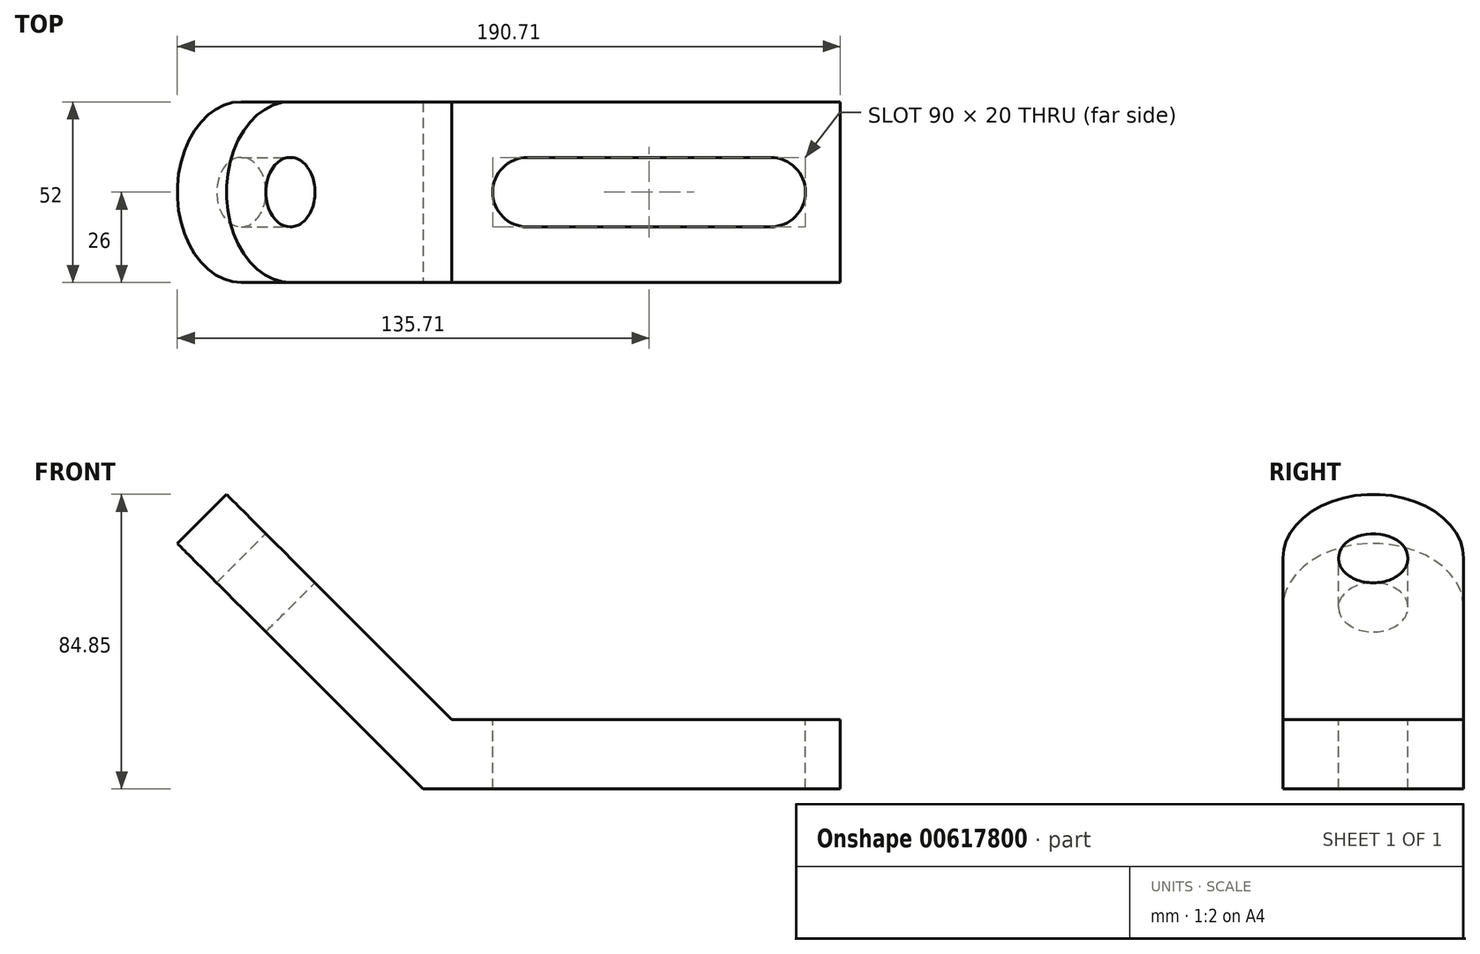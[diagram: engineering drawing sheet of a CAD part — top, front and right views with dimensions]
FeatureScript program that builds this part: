
annotation { "Feature Type Name" : "Feature", "Feature Type Description" : "" }
export const myFeature = defineFeature(function(context is Context, id is Id, definition is map)
    precondition{}
    {
        {
            var Q0;
            Q0=qCreatedBy(makeId("Top.planeOp"),FACE);
            var sketch = newSketch(context, id + "F0", { "sketchPlane" : qUnion([Q0])});
            skLineSegment(sketch, "E0.bottom", {"start": v(60, 26) * mm, "end": v(-60, 26) * mm});
            skLineSegment(sketch, "E0.top", {"start": v(60, -26) * mm, "end": v(-60, -26) * mm});
            skLineSegment(sketch, "E0.left", {"start": v(60, 26) * mm, "end": v(60, -26) * mm});
            skLineSegment(sketch, "E0.right", {"start": v(-60, 26) * mm, "end": v(-60, -26) * mm});
            skPoint(sketch, "E0.middle", {"position": v(0, 0) * mm});
            skSolve(sketch);
        }
        {
            var Q0;
            Q0=makeQuery(id+"F0.imprint","IMPRINT",FACE,{"disambiguationData":[TD([[makeQuery(id+"F0.imprint","IMPRINT",EDGE,{"derivedFrom":sQuery(id+"F0.wireOp",EDGE,"E0.bottom")}),1.0]])]});
            var sketch = newSketch(context, id + "F1", { "sketchPlane" : qUnion([Q0])});
            skLineSegment(sketch, "E1.bottom", {"start": v(-60, 26) * mm, "end": v(-134, 26) * mm});
            skLineSegment(sketch, "E1.top", {"start": v(-60, -26) * mm, "end": v(-134, -26) * mm});
            skLineSegment(sketch, "E1.left", {"start": v(-60, 26) * mm, "end": v(-60, -26) * mm});
            skLineSegment(sketch, "E1.right", {"start": v(-134, 26) * mm, "end": v(-134, -26) * mm});
            skArc(sketch, "E2", {"start": v(-134, 26) * mm, "mid": v(-160, 0) * mm, "end": v(-134, -26) * mm});
            skSolve(sketch);
        }
        {
            var Q0;
            Q0=makeQuery(id+"F1.imprint","IMPRINT",FACE,{"disambiguationData":[TD([[makeQuery(id+"F1.imprint","IMPRINT",EDGE,{"derivedFrom":sQuery(id+"F1.wireOp",EDGE,"E1.bottom")}),1.0]])]});
            var Q1;
            Q1=makeQuery(id+"F1.imprint","IMPRINT",FACE,{"disambiguationData":[TD([[makeQuery(id+"F1.imprint","IMPRINT",EDGE,{"derivedFrom":sQuery(id+"F1.wireOp",EDGE,"E1.right")}),-1.0]])]});
            extrude(context, id + "F2", {"entities" : qUnion([Q0, Q1]), "depth" : 20 * mm, "offsetDistance" : 25 * mm});
        }
        {
            var Q0;
            Q0=makeQuery(id+"F2.opExtrude","SWEPT_BODY",BODY,{"disambiguationData":[OSD([sQuery(id+"F1.wireOp",EDGE,"E1.bottom"),sQuery(id+"F1.wireOp",EDGE,"E1.top"),sQuery(id+"F1.wireOp",EDGE,"E1.left"),sQuery(id+"F1.wireOp",EDGE,"E1.right")])]});
            var Q1;
            Q1=sQuery(id+"F0.wireOp",EDGE,"E0.right");
            transform(context, id + "F3", {"entities" : qUnion([Q0]), "transformType" : TransformType.ROTATION, "transformAxis" : qUnion([Q1]), "angle" : 45 * degree, "oppositeDirection" : true, "makeCopy" : false});
        }
        {
            var Q0;
            Q0=makeQuery(id+"F0.imprint","IMPRINT",FACE,{"disambiguationData":[TD([[makeQuery(id+"F0.imprint","IMPRINT",EDGE,{"derivedFrom":sQuery(id+"F0.wireOp",EDGE,"E0.bottom")}),1.0]])]});
            extrude(context, id + "F4", {"entities" : qUnion([Q0]), "operationType" : NewBodyOperationType.ADD, "depth" : 20 * mm, "offsetDistance" : 25 * mm});
        }
        {
            var Q0;
            Q0=makeQuery(id+"F4.opExtrude","CAP_FACE",FACE,{"disambiguationData":[OSD([sQuery(id+"F0.wireOp",EDGE,"E0.bottom"),sQuery(id+"F0.wireOp",EDGE,"E0.top"),sQuery(id+"F0.wireOp",EDGE,"E0.left"),sQuery(id+"F0.wireOp",EDGE,"E0.right")])],"isStart":false});
            var sketch = newSketch(context, id + "F5", { "sketchPlane" : qUnion([Q0])});
            skLineSegment(sketch, "E3.bottom", {"start": v(-30, 10) * mm, "end": v(40, 10) * mm});
            skLineSegment(sketch, "E3.top", {"start": v(-30, -10) * mm, "end": v(40, -10) * mm});
            skLineSegment(sketch, "E3.left", {"start": v(-30, 10) * mm, "end": v(-30, -10) * mm});
            skLineSegment(sketch, "E3.right", {"start": v(40, 10) * mm, "end": v(40, -10) * mm});
            skPoint(sketch, "E3.middle", {"position": v(5, 0) * mm});
            skArc(sketch, "E4", {"start": v(40, -10) * mm, "mid": v(50, 0) * mm, "end": v(40, 10) * mm});
            skArc(sketch, "E5", {"start": v(-30, 10) * mm, "mid": v(-40, 0) * mm, "end": v(-30, -10) * mm});
            skSolve(sketch);
        }
        {
            var Q0;
            Q0 = qSketchRegion(id + "F5", true);
            extrude(context, id + "F6", {"entities" : qUnion([Q0]), "operationType" : NewBodyOperationType.REMOVE, "oppositeDirection" : true, "depth" : 20 * mm, "offsetDistance" : 25 * mm});
        }
        {
            var Q0;
            Q0=makeQuery(id+"F2.opExtrude","CAP_FACE",FACE,{"disambiguationData":[OSD([sQuery(id+"F1.wireOp",EDGE,"E1.bottom"),sQuery(id+"F1.wireOp",EDGE,"E1.top"),sQuery(id+"F1.wireOp",EDGE,"E1.left"),sQuery(id+"F1.wireOp",EDGE,"E2")])],"isStart":false});
            var sketch = newSketch(context, id + "F7", { "sketchPlane" : qUnion([Q0])});
            skCircle(sketch, "E6", {"center": v(0, 116.43) * mm, "radius": 10 * mm});
            skSolve(sketch);
        }
        {
            var Q0;
            Q0 = qSketchRegion(id + "F7", true);
            extrude(context, id + "F8", {"entities" : qUnion([Q0]), "operationType" : NewBodyOperationType.REMOVE, "oppositeDirection" : true, "depth" : 25 * mm, "offsetDistance" : 25 * mm});
        }
    });
